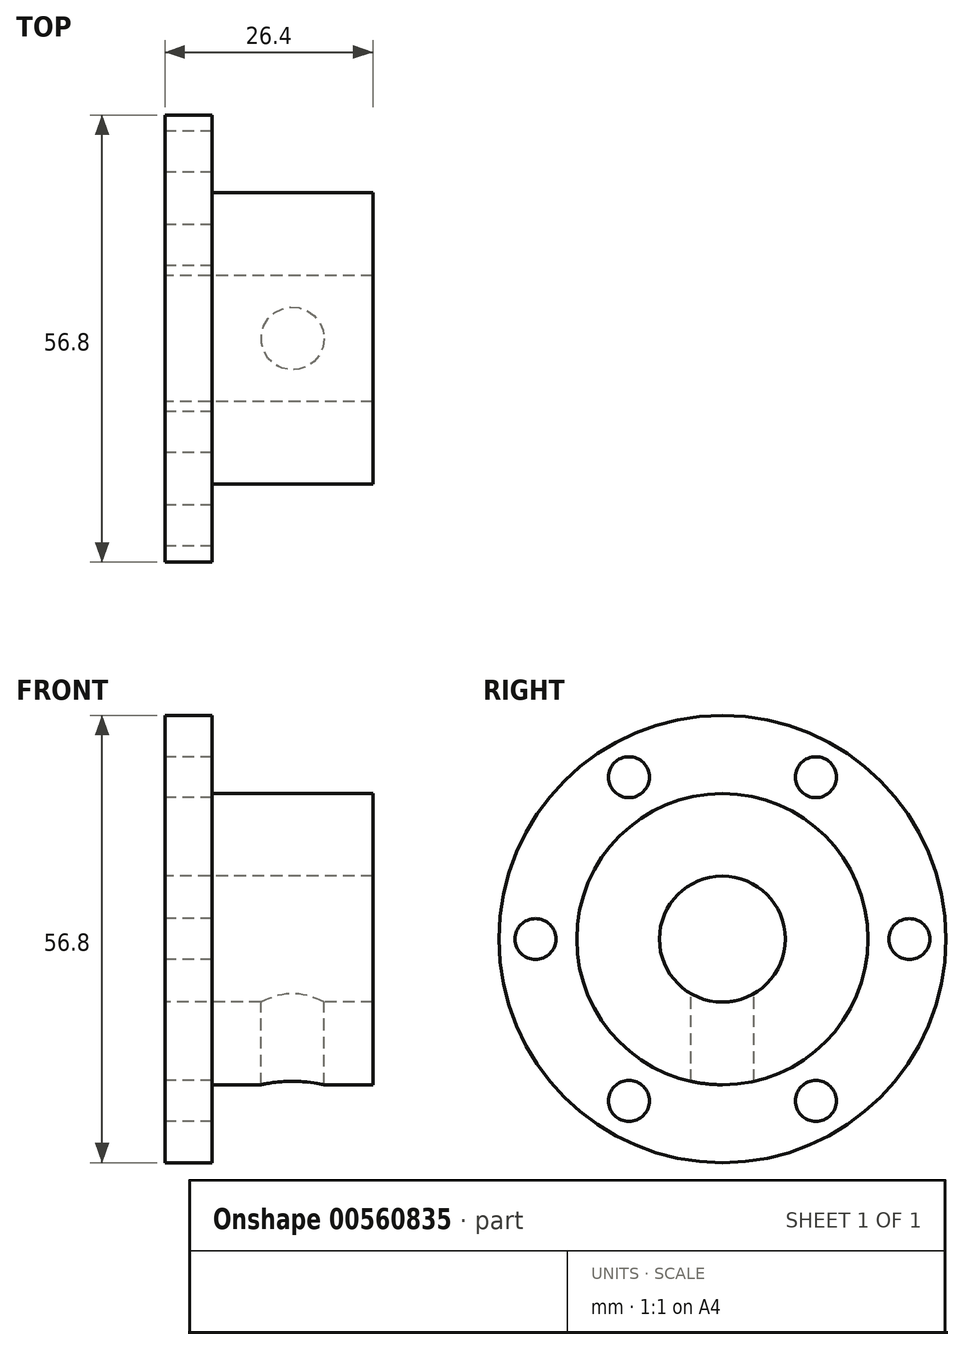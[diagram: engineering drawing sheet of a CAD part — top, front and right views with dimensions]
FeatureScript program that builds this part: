
annotation { "Feature Type Name" : "Feature", "Feature Type Description" : "" }
export const myFeature = defineFeature(function(context is Context, id is Id, definition is map)
    precondition{}
    {
        {
            var Q0;
            Q0=qCreatedBy(makeId("Front.planeOp"),FACE);
            var sketch = newSketch(context, id + "F0", { "sketchPlane" : qUnion([Q0])});
            skLineSegment(sketch, "E0", {"start": v(0, 0) * mm, "end": v(116.92, 0) * mm});
            skLineSegment(sketch, "E1", {"start": v(0, 0) * mm, "end": v(0, 8) * mm});
            skLineSegment(sketch, "E2", {"start": v(0, 8) * mm, "end": v(0, 28.4) * mm});
            skLineSegment(sketch, "E3", {"start": v(0, 28.4) * mm, "end": v(6, 28.4) * mm});
            skLineSegment(sketch, "E4", {"start": v(6, 28.4) * mm, "end": v(6, 18.5) * mm});
            skLineSegment(sketch, "E5", {"start": v(6, 18.5) * mm, "end": v(26.4, 18.5) * mm});
            skLineSegment(sketch, "E6", {"start": v(0, 8) * mm, "end": v(26.4, 8) * mm});
            skLineSegment(sketch, "E7", {"start": v(26.4, 8) * mm, "end": v(26.4, 18.5) * mm});
            skSolve(sketch);
        }
        {
            var Q0;
            Q0=qSketchRegion(id+"F0",true);
            var Q1;
            Q1=sQuery(id+"F0.wireOp",EDGE,"E0");
            revolve(context, id + "F1", {"entities" : qUnion([Q0]), "axis" : qUnion([Q1]), "revolveType" : RevolveType.FULL});
        }
        {
            var Q0;
            Q0=qCreatedBy(makeId("Right.planeOp"),FACE);
            var sketch = newSketch(context, id + "F2", { "sketchPlane" : qUnion([Q0])});
            skLineSegment(sketch, "E8", {"start": v(0, 0) * mm, "end": v(-28.29, 0) * mm, "construction": true});
            skCircle(sketch, "E9", {"center": v(0, 0) * mm, "radius": 23.75 * mm, "construction": true});
            skCircle(sketch, "E10", {"center": v(-23.75, 0) * mm, "radius": 2.6 * mm});
            skCircle(sketch, "E11.1.0", {"center": v(-11.88, -20.57) * mm, "radius": 2.6 * mm});
            skCircle(sketch, "E11.2.0", {"center": v(11.87, -20.57) * mm, "radius": 2.6 * mm});
            skCircle(sketch, "E11.3.0", {"center": v(23.75, 0) * mm, "radius": 2.6 * mm});
            skCircle(sketch, "E11.4.0", {"center": v(11.88, 20.57) * mm, "radius": 2.6 * mm});
            skCircle(sketch, "E11.5.0", {"center": v(-11.88, 20.57) * mm, "radius": 2.6 * mm});
            skSolve(sketch);
        }
        {
            var Q0;
            Q0=makeQuery(id+"F2.imprint","IMPRINT",FACE,{"disambiguationData":[TD([[makeQuery(id+"F2.imprint","IMPRINT",EDGE,{"derivedFrom":sQuery(id+"F2.wireOp",EDGE,"E11.4.0")}),1.0]])]});
            var Q1;
            Q1=makeQuery(id+"F2.imprint","IMPRINT",FACE,{"disambiguationData":[TD([[makeQuery(id+"F2.imprint","IMPRINT",EDGE,{"derivedFrom":sQuery(id+"F2.wireOp",EDGE,"E11.3.0")}),1.0]])]});
            var Q2;
            Q2=makeQuery(id+"F2.imprint","IMPRINT",FACE,{"disambiguationData":[TD([[makeQuery(id+"F2.imprint","IMPRINT",EDGE,{"derivedFrom":sQuery(id+"F2.wireOp",EDGE,"E11.2.0")}),1.0]])]});
            var Q3;
            Q3=makeQuery(id+"F2.imprint","IMPRINT",FACE,{"disambiguationData":[TD([[makeQuery(id+"F2.imprint","IMPRINT",EDGE,{"derivedFrom":sQuery(id+"F2.wireOp",EDGE,"E11.1.0")}),1.0]])]});
            var Q4;
            Q4=makeQuery(id+"F2.imprint","IMPRINT",FACE,{"disambiguationData":[TD([[makeQuery(id+"F2.imprint","IMPRINT",EDGE,{"derivedFrom":sQuery(id+"F2.wireOp",EDGE,"E10")}),1.0]])]});
            var Q5;
            Q5=makeQuery(id+"F2.imprint","IMPRINT",FACE,{"disambiguationData":[TD([[makeQuery(id+"F2.imprint","IMPRINT",EDGE,{"derivedFrom":sQuery(id+"F2.wireOp",EDGE,"E11.5.0")}),1.0]])]});
            var Q6;
            Q6=sQuery(id+"F2.wireOp",EDGE,"E11.3.0");
            var Q7;
            Q7=sQuery(id+"F2.wireOp",EDGE,"E11.2.0");
            var Q8;
            Q8=sQuery(id+"F2.wireOp",EDGE,"E11.1.0");
            var Q9;
            Q9=sQuery(id+"F2.wireOp",EDGE,"E10");
            var Q10;
            Q10=sQuery(id+"F2.wireOp",EDGE,"E11.4.0");
            var Q11;
            Q11=sQuery(id+"F2.wireOp",EDGE,"E11.5.0");
            extrude(context, id + "F3", {"entities" : qUnion([Q0, Q1, Q2, Q3, Q4, Q5]), "operationType" : NewBodyOperationType.REMOVE, "surfaceEntities" : qUnion([Q6, Q7, Q8, Q9, Q10, Q11]), "endBound" : BoundingType.UP_TO_NEXT, "depth" : 25 * mm, "offsetDistance" : 25 * mm});
        }
        {
            var Q0;
            Q0=qCreatedBy(makeId("Top.planeOp"),FACE);
            var sketch = newSketch(context, id + "F4", { "sketchPlane" : qUnion([Q0])});
            skLineSegment(sketch, "E12", {"start": v(0, 0) * mm, "end": v(16.2, 0) * mm, "construction": true});
            skCircle(sketch, "E13", {"center": v(16.2, 0) * mm, "radius": 4 * mm});
            skSolve(sketch);
        }
        {
            var Q0;
            Q0=makeQuery(id+"F4.imprint","IMPRINT",FACE,{"disambiguationData":[TD([[makeQuery(id+"F4.imprint","IMPRINT",EDGE,{"derivedFrom":sQuery(id+"F4.wireOp",EDGE,"E13")}),1.0]])]});
            var Q1;
            Q1=sQuery(id+"F4.wireOp",EDGE,"E13");
            extrude(context, id + "F5", {"entities" : qUnion([Q0]), "operationType" : NewBodyOperationType.REMOVE, "surfaceEntities" : qUnion([Q1]), "endBound" : BoundingType.THROUGH_ALL, "oppositeDirection" : true, "depth" : 25 * mm, "offsetDistance" : 25 * mm});
        }
    });
